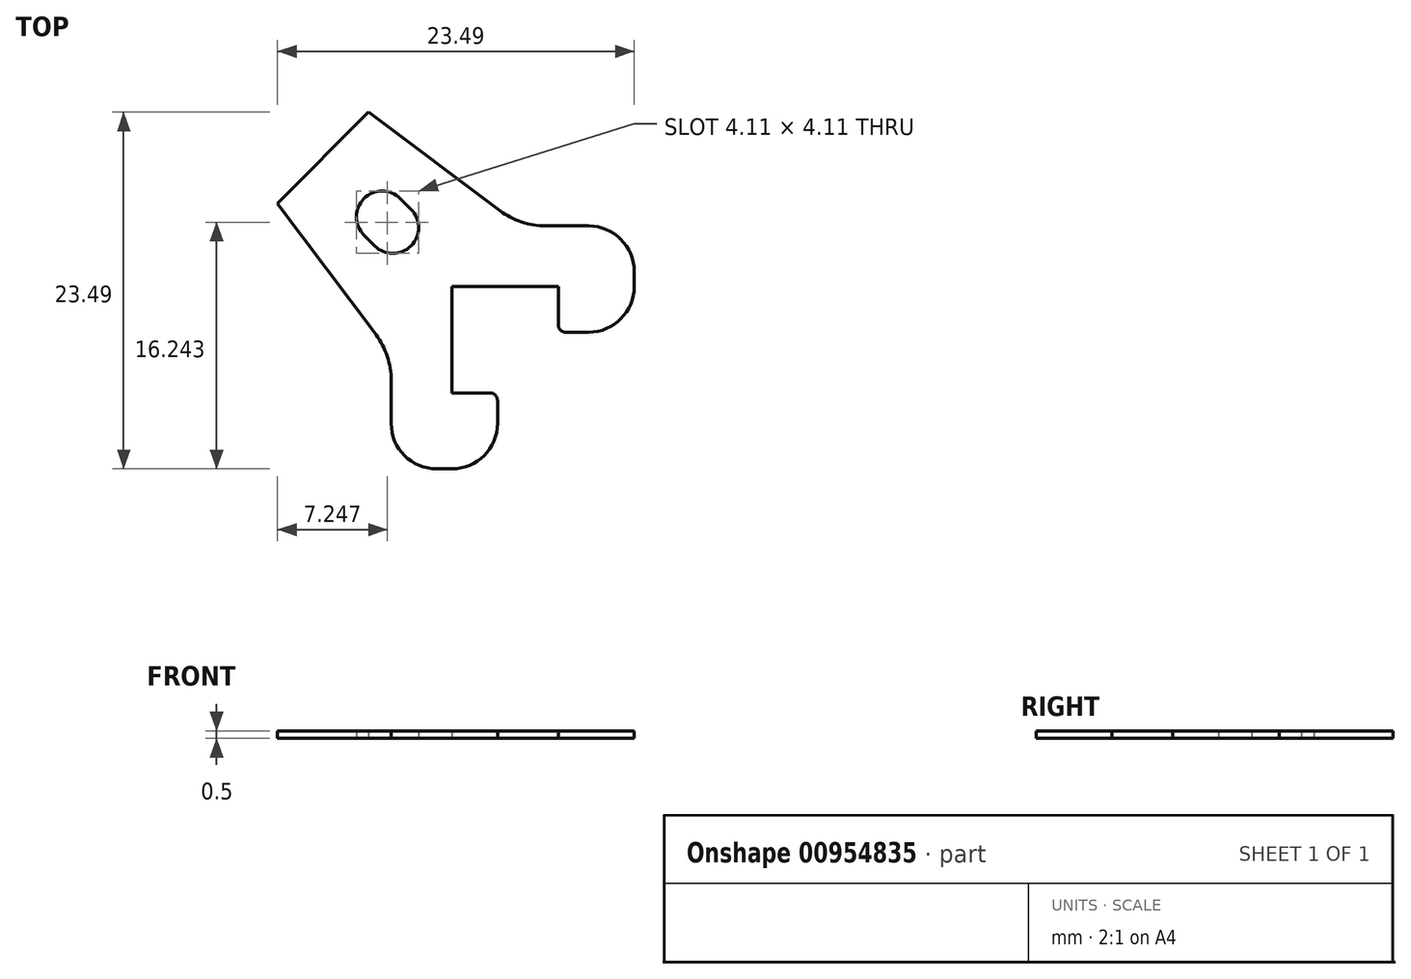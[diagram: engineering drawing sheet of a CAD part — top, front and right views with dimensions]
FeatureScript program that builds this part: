
annotation { "Feature Type Name" : "Feature", "Feature Type Description" : "" }
export const myFeature = defineFeature(function(context is Context, id is Id, definition is map)
    precondition{}
    {
        {
            var Q0;
            Q0=qCreatedBy(makeId("Top.planeOp"),FACE);
            var sketch = newSketch(context, id + "F0", { "sketchPlane" : qUnion([Q0])});
            skLineSegment(sketch, "E0", {"start": v(0, 0) * mm, "end": v(-15.25, 15.25) * mm, "construction": true});
            skLineSegment(sketch, "E1", {"start": v(16.44, 16.44) * mm, "end": v(-16.44, -16.44) * mm, "construction": true});
            skLineSegment(sketch, "E2", {"start": v(-5.48, 11.5) * mm, "end": v(-11.5, 5.48) * mm});
            skLineSegment(sketch, "E3", {"start": v(0, 0) * mm, "end": v(7, 0) * mm});
            skLineSegment(sketch, "E4", {"start": v(7, 0) * mm, "end": v(7, -2.5) * mm});
            skLineSegment(sketch, "E5", {"start": v(7.5, -3) * mm, "end": v(9, -3) * mm});
            skLineSegment(sketch, "E6", {"start": v(12, 0) * mm, "end": v(12, 1) * mm});
            skArc(sketch, "E7", {"start": v(-5.1, 2.69) * mm, "mid": v(-2.69, 2.69) * mm, "end": v(-2.69, 5.1) * mm});
            skArc(sketch, "E8", {"start": v(-3.4, 5.8) * mm, "mid": v(-5.8, 5.8) * mm, "end": v(-5.8, 3.4) * mm});
            skLineSegment(sketch, "E9", {"start": v(-3.4, 5.8) * mm, "end": v(-2.69, 5.1) * mm});
            skLineSegment(sketch, "E10", {"start": v(-5.8, 3.4) * mm, "end": v(-5.1, 2.69) * mm});
            skLineSegment(sketch, "E11.MirrorCS", {"start": v(3, -7.5) * mm, "end": v(3, -9) * mm});
            skLineSegment(sketch, "E12.MirrorCS", {"start": v(0, 0) * mm, "end": v(0, -7) * mm});
            skLineSegment(sketch, "E13.MirrorCS", {"start": v(0, -12) * mm, "end": v(-1, -12) * mm});
            skLineSegment(sketch, "E14.MirrorCS", {"start": v(-16.44, -16.44) * mm, "end": v(16.44, 16.44) * mm, "construction": true});
            skLineSegment(sketch, "E15.MirrorCS", {"start": v(0, -7) * mm, "end": v(2.5, -7) * mm});
            skLineSegment(sketch, "E16", {"start": v(9, 4) * mm, "end": v(6.17, 4) * mm});
            skLineSegment(sketch, "E17", {"start": v(3.17, 5) * mm, "end": v(-5.48, 11.5) * mm});
            skLineSegment(sketch, "E18.MirrorCS", {"start": v(-5, -3.17) * mm, "end": v(-11.5, 5.48) * mm});
            skLineSegment(sketch, "E19.MirrorCS", {"start": v(-4, -9) * mm, "end": v(-4, -6.17) * mm});
            skPoint(sketch, "E20.visualSharp", {"position": v(12, 4) * mm});
            skArc(sketch, "E20.filletArc", {"start": v(12, 1) * mm, "mid": v(11.12, 3.12) * mm, "end": v(9, 4) * mm});
            skPoint(sketch, "E21.visualSharp", {"position": v(12, -3) * mm});
            skArc(sketch, "E21.filletArc", {"start": v(9, -3) * mm, "mid": v(11.12, -2.12) * mm, "end": v(12, 0) * mm});
            skPoint(sketch, "E22.visualSharp", {"position": v(-4, -12) * mm});
            skArc(sketch, "E22.filletArc", {"start": v(-4, -9) * mm, "mid": v(-3.12, -11.12) * mm, "end": v(-1, -12) * mm});
            skPoint(sketch, "E23.visualSharp", {"position": v(3, -12) * mm});
            skArc(sketch, "E23.filletArc", {"start": v(0, -12) * mm, "mid": v(2.12, -11.12) * mm, "end": v(3, -9) * mm});
            skPoint(sketch, "E24.visualSharp", {"position": v(4.5, 4) * mm});
            skArc(sketch, "E24.filletArc", {"start": v(3.17, 5) * mm, "mid": v(4.59, 4.26) * mm, "end": v(6.17, 4) * mm});
            skPoint(sketch, "E25.visualSharp", {"position": v(-4, -4.5) * mm});
            skArc(sketch, "E25.filletArc", {"start": v(-4, -6.17) * mm, "mid": v(-4.26, -4.59) * mm, "end": v(-5, -3.17) * mm});
            skPoint(sketch, "E26.visualSharp", {"position": v(7, -3) * mm});
            skArc(sketch, "E26.filletArc", {"start": v(7, -2.5) * mm, "mid": v(7.15, -2.85) * mm, "end": v(7.5, -3) * mm});
            skPoint(sketch, "E27.visualSharp", {"position": v(3, -7) * mm});
            skArc(sketch, "E27.filletArc", {"start": v(3, -7.5) * mm, "mid": v(2.85, -7.15) * mm, "end": v(2.5, -7) * mm});
            skSolve(sketch);
        }
        {
            var Q0;
            Q0=makeQuery(id+"F0.imprint","IMPRINT",FACE,{"disambiguationData":[TD([[makeQuery(id+"F0.imprint","IMPRINT",EDGE,{"derivedFrom":sQuery(id+"F0.wireOp",EDGE,"E2")}),1.0]])]});
            extrude(context, id + "F1", {"entities" : qUnion([Q0]), "depth" : 0.5 * mm, "offsetDistance" : 25 * mm});
        }
    });
